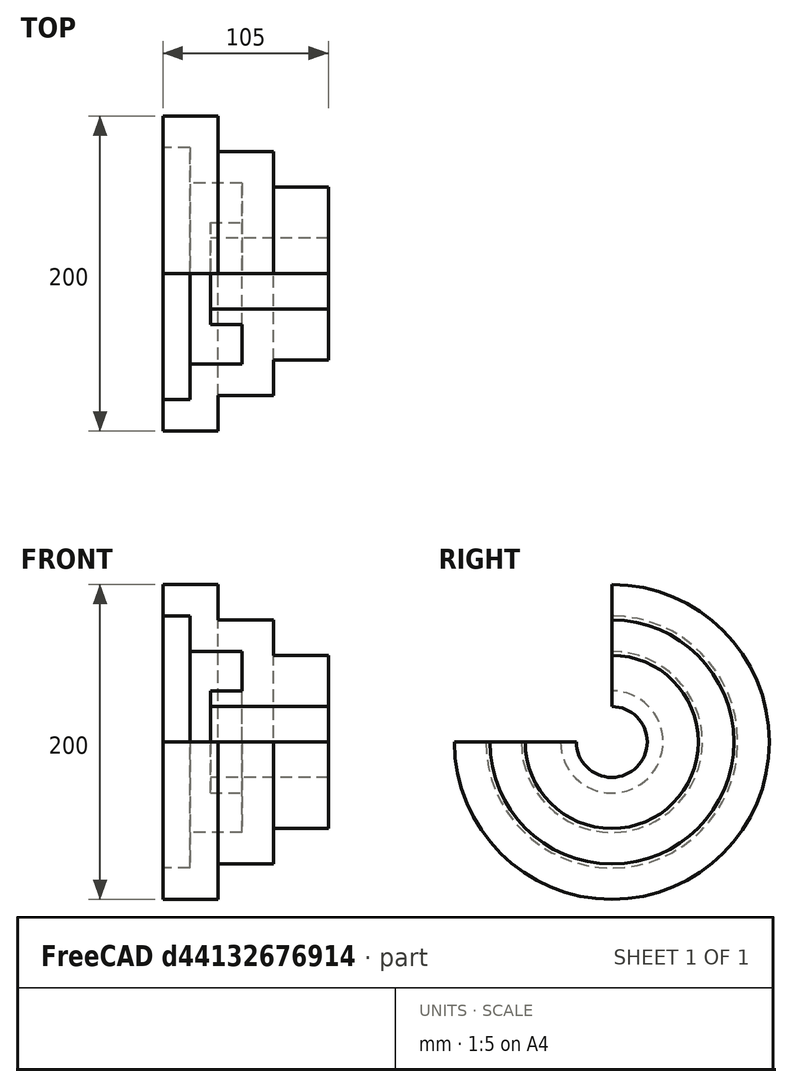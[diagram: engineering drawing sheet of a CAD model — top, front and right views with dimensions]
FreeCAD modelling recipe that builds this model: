
FCSTD DOCUMENT  (FreeCAD 0.16R)
Label: Ejer Final 29
License: All rights reserved
LicenseURL: http://en.wikipedia.org/wiki/All_rights_reserved
objects: Sketcher::SketchObject×1, PartDesign::Revolution×1
note: 3 computed .brp shape members not serialized (recipe doc carries the construction recipe); baked Part::Feature solids carry a one-line shape summary decoded from their .brp

FEATURE [Sketcher::SketchObject] Sketch
  sketch-geometry (14):
    g0: LineSegment StartX=0 StartY=-22.5 StartZ=0 EndX=-75 EndY=-22.5 EndZ=0
    g1: LineSegment StartX=-75 StartY=-22.5 StartZ=0 EndX=-75 EndY=-32.5 EndZ=0
    g2: LineSegment StartX=-75 StartY=-32.5 StartZ=0 EndX=-55 EndY=-32.5 EndZ=0
    g3: LineSegment StartX=-55 StartY=-32.5 StartZ=0 EndX=-55 EndY=-57.5 EndZ=0
    g4: LineSegment StartX=-55 StartY=-57.5 StartZ=0 EndX=-88 EndY=-57.5 EndZ=0
    g5: LineSegment StartX=-88 StartY=-57.5 StartZ=0 EndX=-88 EndY=-80 EndZ=0
    g6: LineSegment StartX=-88 StartY=-80 StartZ=0 EndX=-105 EndY=-80 EndZ=0
    g7: LineSegment StartX=-105 StartY=-80 StartZ=0 EndX=-105 EndY=-100 EndZ=0
    g8: LineSegment StartX=-105 StartY=-100 StartZ=0 EndX=-70 EndY=-100 EndZ=0
    g9: LineSegment StartX=-70 StartY=-100 StartZ=0 EndX=-70 EndY=-77.5 EndZ=0
    g10: LineSegment StartX=-70 StartY=-77.5 StartZ=0 EndX=-35 EndY=-77.5 EndZ=0
    g11: LineSegment StartX=-35 StartY=-77.5 StartZ=0 EndX=-35 EndY=-55 EndZ=0
    g12: LineSegment StartX=-35 StartY=-55 StartZ=0 EndX=0 EndY=-55 EndZ=0
    g13: LineSegment StartX=0 StartY=-55 StartZ=0 EndX=0 EndY=-22.5 EndZ=0
  constraints (42):
    c: PointOnObject(g0,g-2)
    c: Horizontal(g0)
    c: Coincident(g0,g1)
    c: Vertical(g1)
    c: DistanceY(g0,g-1) = 22.5
    c: DistanceX(g0,g0) = 75
    c: DistanceY(g1,g-1) = 32.5
    c: Coincident(g2,g1)
    c: Horizontal(g2)
    c: Coincident(g2,g3)
    c: DistanceY(g3,g-1) = 57.5
    c: Coincident(g4,g3)
    c: Horizontal(g4)
    c: DistanceX(g4,g4) = 33
    c: Vertical(g3)
    c: Coincident(g5,g4)
    c: Vertical(g5)
    c: DistanceY(g5,g-1) = 80
    c: Coincident(g5,g6)
    c: Horizontal(g6)
    c: Coincident(g6,g7)
    c: Vertical(g7)
    c: DistanceX(g6,g5) = 17
    c: DistanceY(g7,g-1) = 100
    c: Coincident(g8,g7)
    c: Horizontal(g8)
    c: DistanceX(g8,g8) = 35
    c: Coincident(g9,g8)
    c: Vertical(g9)
    c: DistanceY(g9,g-1) = 77.5
    c: Coincident(g10,g9)
    c: Horizontal(g10)
    c: DistanceX(g10,g10) = 35
    c: Coincident(g11,g10)
    c: Vertical(g11)
    c: DistanceY(g11,g-1) = 55
    c: Coincident(g12,g11)
    c: Horizontal(g12)
    c: DistanceX(g11,g12) = 35
    c: Coincident(g13,g12)
    c: Coincident(g13,g0)
    c: Vertical(g13)
FEATURE [PartDesign::Revolution] Revolution
  Angle = 270
  Axis = (1,0,0)
  Base = (0,0,0)
  ReferenceAxis = -> Sketch [H_Axis]
  Sketch = -> Sketch
